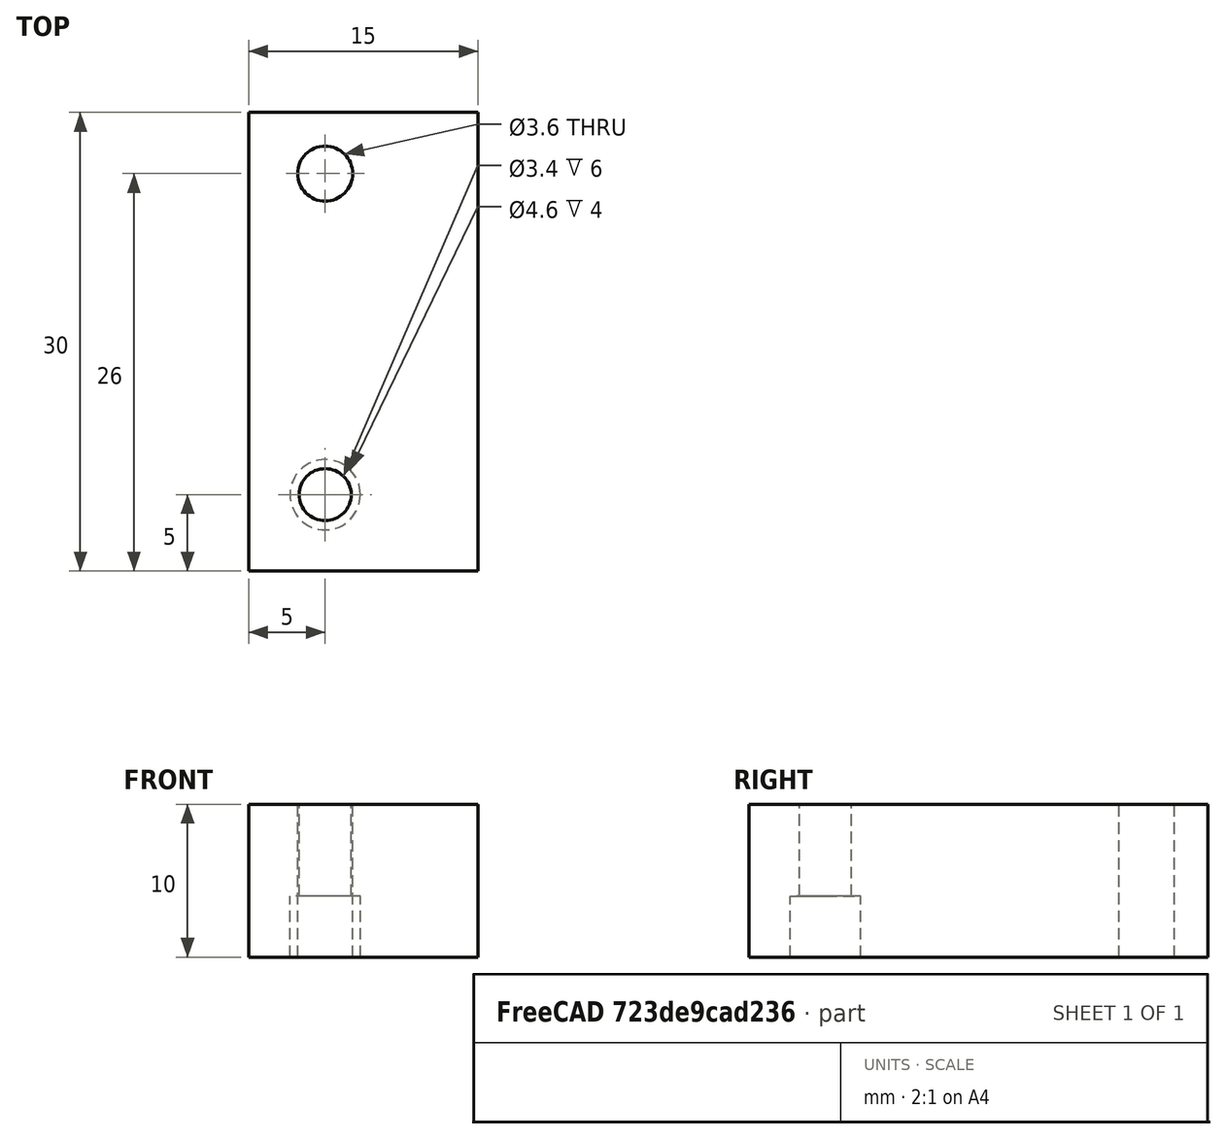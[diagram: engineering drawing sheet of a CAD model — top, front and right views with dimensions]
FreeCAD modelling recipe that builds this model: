
FCSTD DOCUMENT  (FreeCAD 0.17R13528 (Git))
Label: photo-led-test
License: All rights reserved
LicenseURL: http://en.wikipedia.org/wiki/All_rights_reserved
objects: Part::Cylinder×3, Part::MultiFuse×2, Part::Box×1, Part::Cut×1
note: 7 computed .brp shape members not serialized (recipe doc carries the construction recipe); baked Part::Feature solids carry a one-line shape summary decoded from their .brp

FEATURE [Part::Cylinder] Cylinder
  Angle = 360
  AttacherType = Attacher::AttachEngine3D
  Height = 10
  Placement = pos=(0,0,7) rot=(0,0,1;0rad)
  Radius = 1.7
FEATURE [Part::Cylinder] Cylinder001
  Angle = 360
  AttacherType = Attacher::AttachEngine3D
  Height = 10
  Radius = 2.3
FEATURE [Part::MultiFuse] Fusion  label="LED-hole"
  Placement = pos=(0,0,-6) rot=(0,0,1;0rad)
  Shapes = -> [Cylinder,Cylinder001]
FEATURE [Part::Box] Box  label="Cube"
  AttacherType = Attacher::AttachEngine3D
  Height = 10
  Length = 15
  Placement = pos=(-5,-5,0) rot=(0,0,1;0rad)
  Width = 30
FEATURE [Part::Cylinder] Cylinder002  label="M3-clear"
  Angle = 360
  AttacherType = Attacher::AttachEngine3D
  Height = 20
  Placement = pos=(0,21,-4) rot=(0,0,1;0rad)
  Radius = 1.8
FEATURE [Part::MultiFuse] Fusion001
  Shapes = -> [Fusion,Cylinder002]
FEATURE [Part::Cut] Cut
  Base = -> Box
  Tool = -> Fusion001
